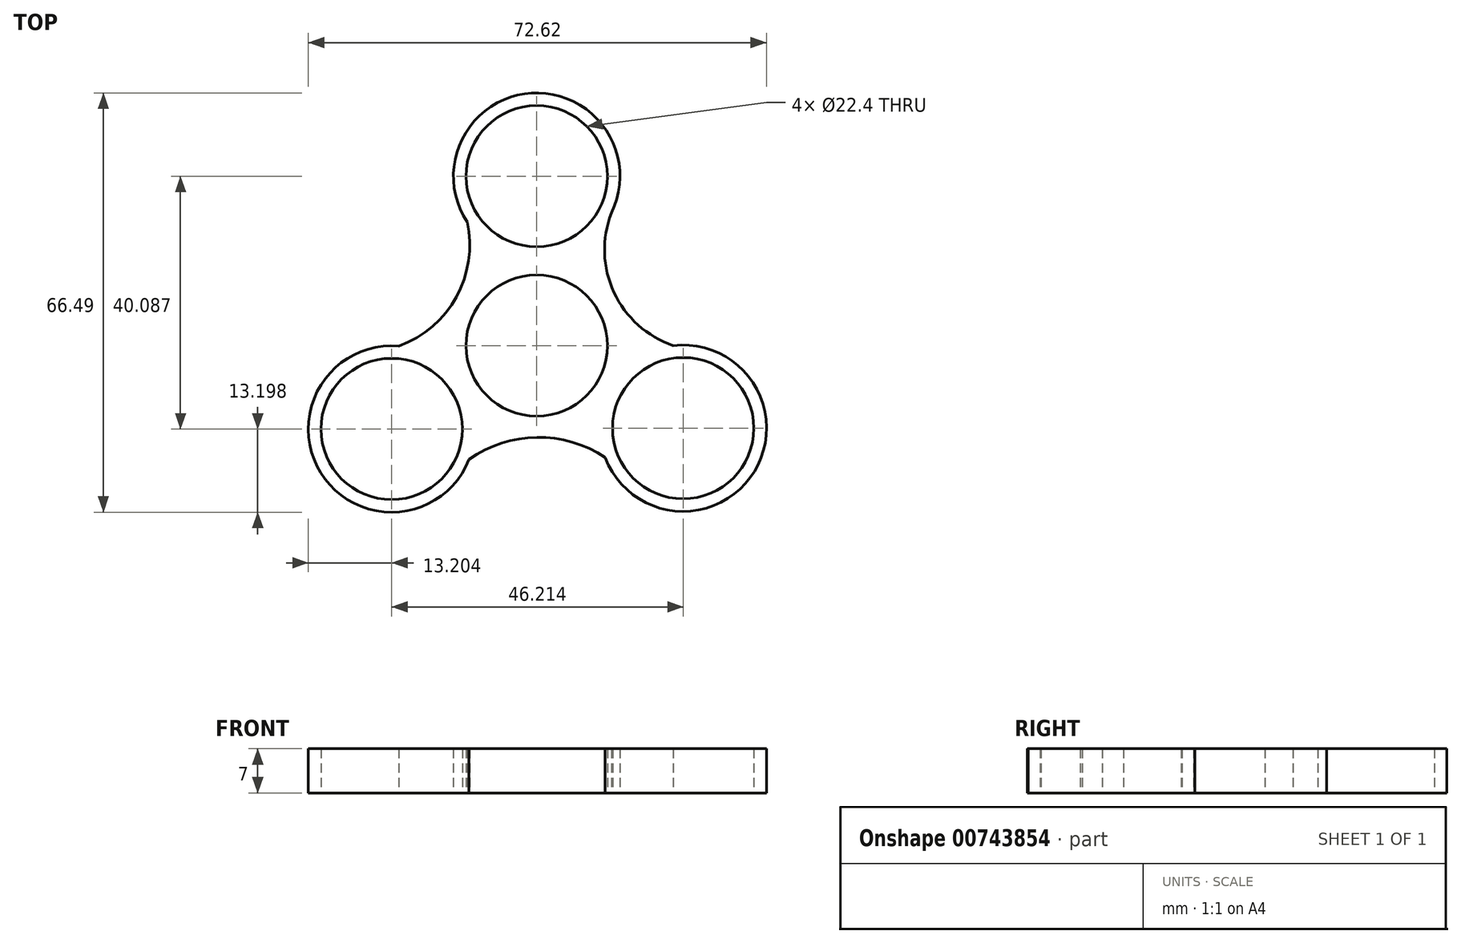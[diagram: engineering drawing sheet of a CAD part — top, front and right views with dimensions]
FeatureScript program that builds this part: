
annotation { "Feature Type Name" : "Feature", "Feature Type Description" : "" }
export const myFeature = defineFeature(function(context is Context, id is Id, definition is map)
    precondition{}
    {
        {
            var Q0;
            Q0=qCreatedBy(makeId("Top.planeOp"),FACE);
            var sketch = newSketch(context, id + "F0", { "sketchPlane" : qUnion([Q0])});
            skCircle(sketch, "E0", {"center": v(0, 0) * mm, "radius": 11.2 * mm});
            skCircle(sketch, "E1", {"center": v(0, 26.86) * mm, "radius": 11.2 * mm});
            skArc(sketch, "E2", {"start": v(11.84, 21.03) * mm, "mid": v(-0.82, 40.03) * mm, "end": v(-11.03, 19.6) * mm});
            skCircle(sketch, "E3.1.0", {"center": v(-23, -13.23) * mm, "radius": 11.2 * mm});
            skArc(sketch, "E3.1.1", {"start": v(-21.84, -0.08) * mm, "mid": v(-34.22, -20.17) * mm, "end": v(-10.72, -18.07) * mm});
            skCircle(sketch, "E3.2.0", {"center": v(23.22, -13.1) * mm, "radius": 11.2 * mm});
            skArc(sketch, "E3.2.1", {"start": v(10.86, -17.75) * mm, "mid": v(34.5, -19.95) * mm, "end": v(21.63, 0) * mm});
            skPoint(sketch, "E3.center", {"position": v(0.07, 0.17) * mm});
            skArc(sketch, "E4", {"start": v(11.84, 21.03) * mm, "mid": v(12.26, 8.43) * mm, "end": v(21.63, 0) * mm});
            skArc(sketch, "E5", {"start": v(10.86, -17.75) * mm, "mid": v(0.02, -14.54) * mm, "end": v(-10.72, -18.07) * mm});
            skArc(sketch, "E6", {"start": v(-21.84, -0.08) * mm, "mid": v(-12.73, 7.73) * mm, "end": v(-11.03, 19.6) * mm});
            skSolve(sketch);
        }
        {
            var Q0;
            Q0=makeQuery(id+"F0.imprint","IMPRINT",FACE,{"disambiguationData":[TD([[makeQuery(id+"F0.imprint","IMPRINT",EDGE,{"derivedFrom":sQuery(id+"F0.wireOp",EDGE,"E0")}),-1.0]])]});
            extrude(context, id + "F1", {"entities" : qUnion([Q0]), "depth" : 7 * mm, "offsetDistance" : 25 * mm});
        }
    });
